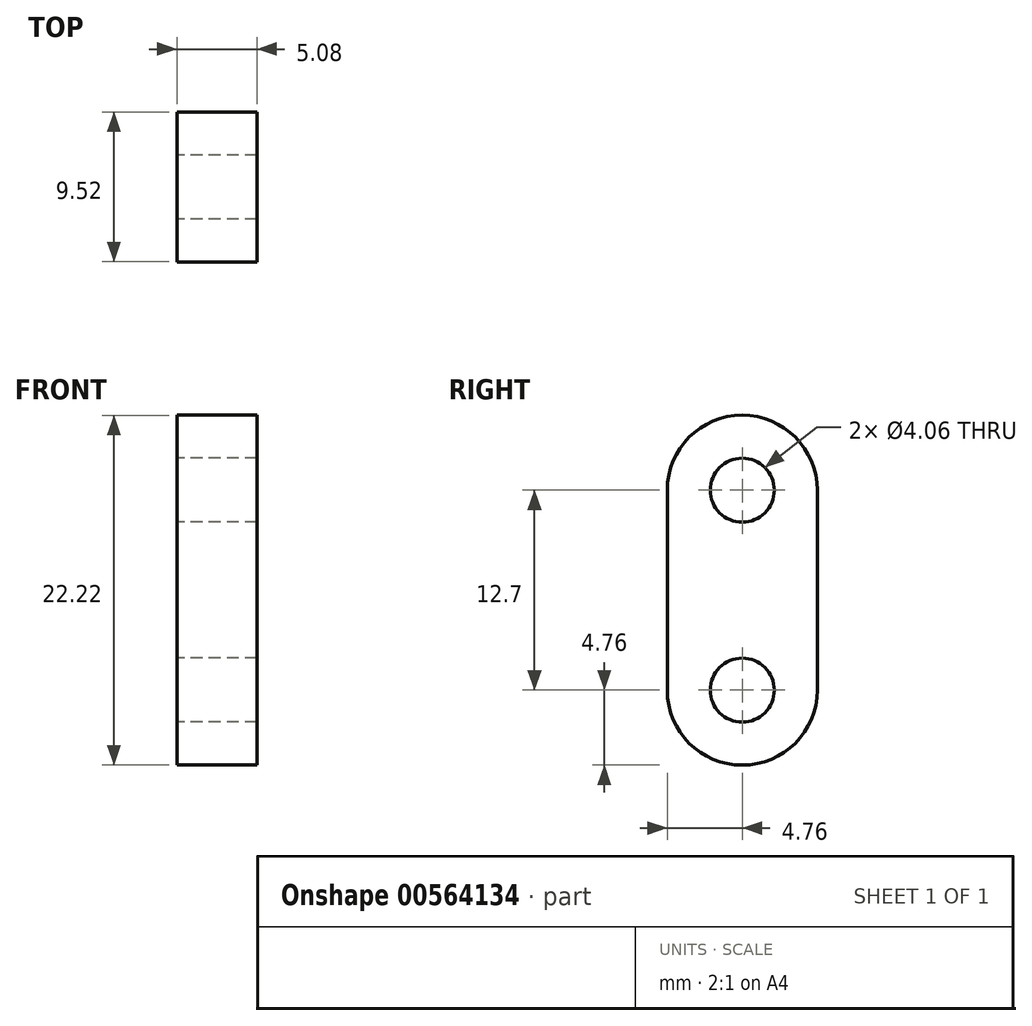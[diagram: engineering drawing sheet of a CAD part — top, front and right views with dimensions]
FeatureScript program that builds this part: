
annotation { "Feature Type Name" : "Feature", "Feature Type Description" : "" }
export const myFeature = defineFeature(function(context is Context, id is Id, definition is map)
    precondition{}
    {
        {
            var Q0;
            Q0=qCreatedBy(makeId("Right.planeOp"),FACE);
            var sketch = newSketch(context, id + "F0", { "sketchPlane" : qUnion([Q0])});
            skCircle(sketch, "E0", {"center": v(0, 0) * mm, "radius": 4.76 * mm});
            skCircle(sketch, "E1", {"center": v(0, 12.7) * mm, "radius": 4.76 * mm});
            skCircle(sketch, "E2", {"center": v(0, 0) * mm, "radius": 2.03 * mm});
            skCircle(sketch, "E3", {"center": v(0, 12.7) * mm, "radius": 2.03 * mm});
            skLineSegment(sketch, "E4", {"start": v(-4.76, 12.7) * mm, "end": v(-4.76, 0) * mm});
            skLineSegment(sketch, "E5", {"start": v(4.76, 12.7) * mm, "end": v(4.76, 0) * mm});
            skSolve(sketch);
        }
        {
            var Q0;
            Q0 = qSketchRegion(id + "F0", true);
            extrude(context, id + "F1", {"entities" : qUnion([Q0]), "depth" : 5.08 * mm, "offsetDistance" : 25.4 * mm});
        }
    });
